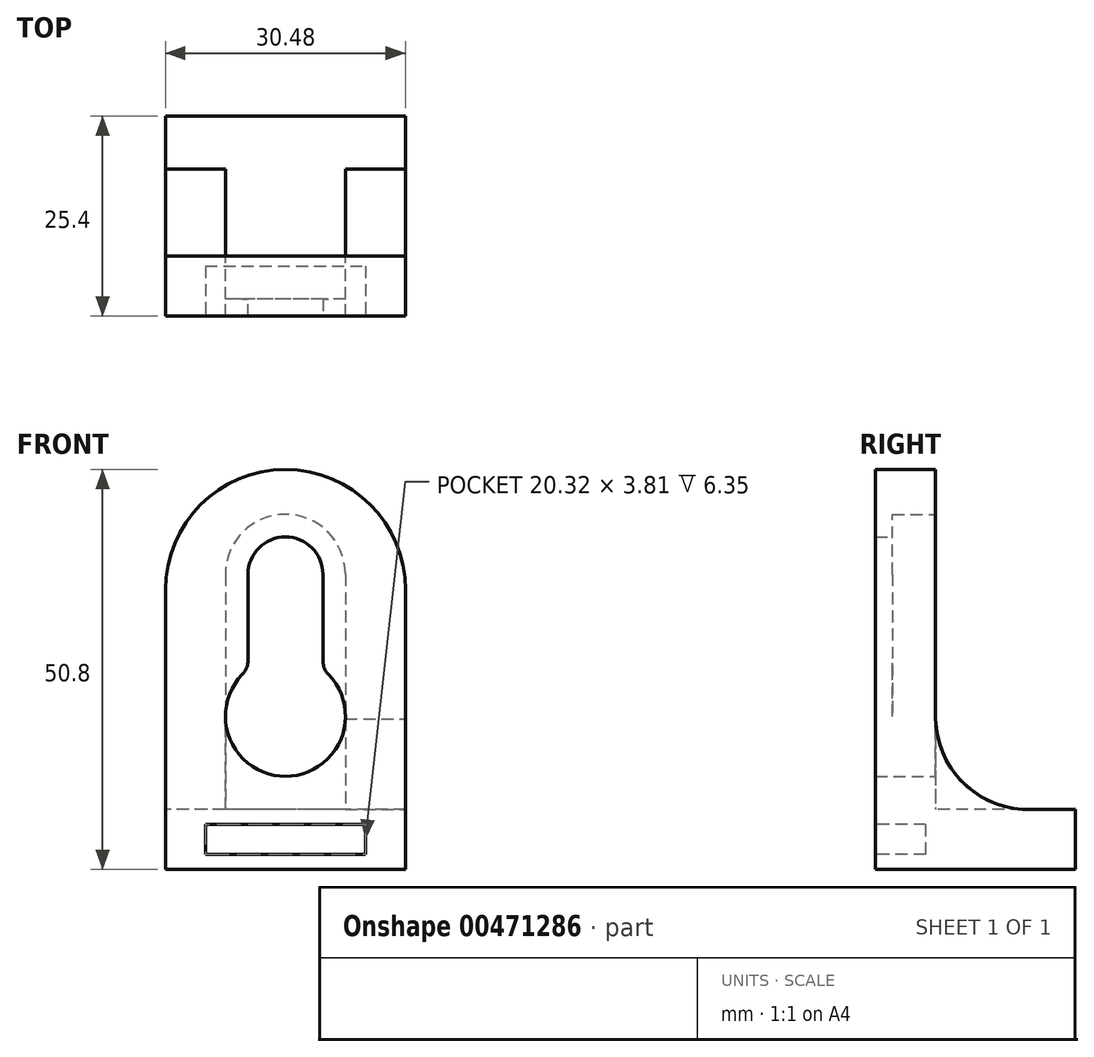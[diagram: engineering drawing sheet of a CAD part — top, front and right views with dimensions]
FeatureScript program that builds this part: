
annotation { "Feature Type Name" : "Feature", "Feature Type Description" : "" }
export const myFeature = defineFeature(function(context is Context, id is Id, definition is map)
    precondition{}
    {
        {
            var Q0;
            Q0=qCreatedBy(makeId("Front.planeOp"),FACE);
            var sketch = newSketch(context, id + "F0", { "sketchPlane" : qUnion([Q0])});
            skLineSegment(sketch, "E0.bottom", {"start": v(-15.24, 25.4) * mm, "end": v(15.24, 25.4) * mm});
            skLineSegment(sketch, "E0.top", {"start": v(-15.24, -25.4) * mm, "end": v(15.24, -25.4) * mm});
            skLineSegment(sketch, "E0.left", {"start": v(-15.24, 25.4) * mm, "end": v(-15.24, -25.4) * mm});
            skLineSegment(sketch, "E0.right", {"start": v(15.24, 25.4) * mm, "end": v(15.24, -25.4) * mm});
            skSolve(sketch);
        }
        {
            var Q0;
            Q0=makeQuery(id+"F0.imprint","IMPRINT",FACE,{"disambiguationData":[TD([[makeQuery(id+"F0.imprint","IMPRINT",EDGE,{"derivedFrom":sQuery(id+"F0.wireOp",EDGE,"E0.bottom")}),-1.0]])]});
            var sketch = newSketch(context, id + "F1", { "sketchPlane" : qUnion([Q0])});
            skArc(sketch, "E1", {"start": v(4.76, 12.09) * mm, "mid": v(0, 16.85) * mm, "end": v(-4.76, 12.09) * mm});
            skArc(sketch, "E2", {"start": v(-4.76, 0) * mm, "mid": v(0, -13.57) * mm, "end": v(4.76, 0) * mm});
            skLineSegment(sketch, "E3", {"start": v(-4.76, 12.09) * mm, "end": v(-4.76, 0) * mm});
            skLineSegment(sketch, "E4", {"start": v(4.76, 12.09) * mm, "end": v(4.76, 0) * mm});
            skArc(sketch, "E5", {"start": v(7.62, 12.09) * mm, "mid": v(0, 19.7) * mm, "end": v(-7.62, 12.09) * mm});
            skLineSegment(sketch, "E6", {"start": v(-7.62, 12.09) * mm, "end": v(-7.62, -5.95) * mm});
            skLineSegment(sketch, "E7", {"start": v(7.62, 12.09) * mm, "end": v(7.62, -5.95) * mm});
            skSolve(sketch);
        }
        {
            var Q0;
            Q0 = qSketchRegion(id + "F0", true);
            extrude(context, id + "F2", {"entities" : qUnion([Q0]), "depth" : 7.62 * mm, "offsetDistance" : 25.4 * mm});
        }
        {
            var Q0;
            Q0=makeQuery(id+"F1.imprint","IMPRINT",FACE,{"disambiguationData":[TD([[makeQuery(id+"F1.imprint","IMPRINT",EDGE,{"derivedFrom":sQuery(id+"F1.wireOp",EDGE,"E1")}),1.0]])]});
            extrude(context, id + "F3", {"entities" : qUnion([Q0]), "operationType" : NewBodyOperationType.REMOVE, "depth" : 7.62 * mm, "offsetDistance" : 25.4 * mm});
        }
        {
            var Q0;
            Q0 = qSketchRegion(id + "F1", true);
            extrude(context, id + "F4", {"entities" : qUnion([Q0]), "operationType" : NewBodyOperationType.REMOVE, "depth" : 5.46 * mm, "offsetDistance" : 25.4 * mm});
        }
        {
            var Q0;
            Q0=makeQuery(id+"F2.opExtrude","CAP_FACE",FACE,{"disambiguationData":[OSD([sQuery(id+"F0.wireOp",EDGE,"E0.bottom"),sQuery(id+"F0.wireOp",EDGE,"E0.top"),sQuery(id+"F0.wireOp",EDGE,"E0.left"),sQuery(id+"F0.wireOp",EDGE,"E0.right")])],"isStart":true});
            var sketch = newSketch(context, id + "F5", { "sketchPlane" : qUnion([Q0])});
            skLineSegment(sketch, "E8.bottom", {"start": v(-15.24, -25.4) * mm, "end": v(15.24, -25.4) * mm});
            skLineSegment(sketch, "E8.top", {"start": v(-15.24, -17.78) * mm, "end": v(15.24, -17.78) * mm});
            skLineSegment(sketch, "E8.left", {"start": v(-15.24, -25.4) * mm, "end": v(-15.24, -17.78) * mm});
            skLineSegment(sketch, "E8.right", {"start": v(15.24, -25.4) * mm, "end": v(15.24, -17.78) * mm});
            skSolve(sketch);
        }
        {
            var Q0;
            Q0 = qSketchRegion(id + "F5", true);
            extrude(context, id + "F6", {"entities" : qUnion([Q0]), "operationType" : NewBodyOperationType.ADD, "depth" : 17.78 * mm, "offsetDistance" : 25.4 * mm});
        }
        {
            var Q0;
            Q0=makeQuery(id+"F6.boolean.opBoolean","MERGE",FACE,{"derivedFrom":[makeQuery(id+"F2.opExtrude","SWEPT_FACE",FACE,{"disambiguationData":[OSD([sQuery(id+"F0.wireOp",EDGE,"E0.right")])]}),makeQuery(id+"F6.opExtrude","SWEPT_FACE",FACE,{"disambiguationData":[OSD([sQuery(id+"F5.wireOp",EDGE,"E8.left")])]})]});
            var sketch = newSketch(context, id + "F7", { "sketchPlane" : qUnion([Q0])});
            skArc(sketch, "E9", {"start": v(0, -6.31) * mm, "mid": v(3.3, -14.18) * mm, "end": v(11.02, -17.78) * mm});
            skLineSegment(sketch, "E10", {"start": v(0, -6.31) * mm, "end": v(0, -17.78) * mm});
            skLineSegment(sketch, "E11", {"start": v(0, -17.78) * mm, "end": v(11.02, -17.78) * mm});
            skSolve(sketch);
        }
        {
            var Q0;
            Q0=makeQuery(id+"F7.imprint","IMPRINT",FACE,{"disambiguationData":[TD([[makeQuery(id+"F7.imprint","IMPRINT",EDGE,{"derivedFrom":sQuery(id+"F7.wireOp",EDGE,"E9")}),-1.0]])]});
            extrude(context, id + "F8", {"entities" : qUnion([Q0]), "operationType" : NewBodyOperationType.ADD, "oppositeDirection" : true, "depth" : 7.62 * mm, "offsetDistance" : 25.4 * mm});
        }
        {
            var Q0;
            Q0=makeQuery(id+"F6.boolean.opBoolean","MERGE",FACE,{"derivedFrom":[makeQuery(id+"F2.opExtrude","SWEPT_FACE",FACE,{"disambiguationData":[OSD([sQuery(id+"F0.wireOp",EDGE,"E0.left")])]}),makeQuery(id+"F6.opExtrude","SWEPT_FACE",FACE,{"disambiguationData":[OSD([sQuery(id+"F5.wireOp",EDGE,"E8.right")])]})]});
            var sketch = newSketch(context, id + "F9", { "sketchPlane" : qUnion([Q0])});
            skLineSegment(sketch, "E12", {"start": v(0, -17.78) * mm, "end": v(-11.02, -17.78) * mm});
            skLineSegment(sketch, "E13", {"start": v(0, -17.78) * mm, "end": v(0, -6) * mm});
            skArc(sketch, "E14", {"start": v(-11.02, -17.78) * mm, "mid": v(-3.19, -14.06) * mm, "end": v(0, -6) * mm});
            skSolve(sketch);
        }
        {
            var Q0;
            Q0=makeQuery(id+"F9.imprint","IMPRINT",FACE,{"disambiguationData":[TD([[makeQuery(id+"F9.imprint","IMPRINT",EDGE,{"derivedFrom":sQuery(id+"F9.wireOp",EDGE,"E12")}),1.0]])]});
            extrude(context, id + "F10", {"entities" : qUnion([Q0]), "operationType" : NewBodyOperationType.ADD, "oppositeDirection" : true, "depth" : 7.62 * mm, "offsetDistance" : 25.4 * mm});
        }
        {
            var Q0;
            Q0=makeQuery(id+"F2.opExtrude","CAP_FACE",FACE,{"disambiguationData":[OSD([sQuery(id+"F0.wireOp",EDGE,"E0.bottom"),sQuery(id+"F0.wireOp",EDGE,"E0.top"),sQuery(id+"F0.wireOp",EDGE,"E0.left"),sQuery(id+"F0.wireOp",EDGE,"E0.right")])],"isStart":false});
            var sketch = newSketch(context, id + "F11", { "sketchPlane" : qUnion([Q0])});
            skLineSegment(sketch, "E15.bottom", {"start": v(-10.16, -19.68) * mm, "end": v(10.16, -19.68) * mm});
            skLineSegment(sketch, "E15.top", {"start": v(-10.16, -23.5) * mm, "end": v(10.16, -23.5) * mm});
            skLineSegment(sketch, "E15.left", {"start": v(-10.16, -19.68) * mm, "end": v(-10.16, -23.5) * mm});
            skLineSegment(sketch, "E15.right", {"start": v(10.16, -19.68) * mm, "end": v(10.16, -23.5) * mm});
            skSolve(sketch);
        }
        {
            var Q0;
            Q0=makeQuery(id+"F11.imprint","IMPRINT",FACE,{"disambiguationData":[TD([[makeQuery(id+"F11.imprint","IMPRINT",EDGE,{"derivedFrom":sQuery(id+"F11.wireOp",EDGE,"E15.bottom")}),-1.0]])]});
            extrude(context, id + "F12", {"entities" : qUnion([Q0]), "operationType" : NewBodyOperationType.REMOVE, "oppositeDirection" : true, "depth" : 6.35 * mm, "offsetDistance" : 25.4 * mm});
        }
        {
            var Q0;
            Q0=makeQuery(id+"F2.opExtrude","SWEPT_EDGE",EDGE,{"disambiguationData":[OSD([sQuery(id+"F0.wireOp",EDGE,"E0.bottom"),sQuery(id+"F0.wireOp",EDGE,"E0.right")])]});
            var Q1;
            Q1=makeQuery(id+"F2.opExtrude","SWEPT_EDGE",EDGE,{"disambiguationData":[OSD([sQuery(id+"F0.wireOp",EDGE,"E0.bottom"),sQuery(id+"F0.wireOp",EDGE,"E0.left")])]});
            fillet(context, id + "F13", {"entities" : qUnion([Q0, Q1]), "radius" : 15.24 * mm, "tangentPropagation" : true, "allowEdgeOverflow" : false});
        }
        {
            var Q0;
            Q0=makeQuery(id+"F3.boolean.opBoolean","COPY",EDGE,{"derivedFrom":makeQuery(id+"F3.opExtrude","SWEPT_EDGE",EDGE,{"disambiguationData":[OSD([sQuery(id+"F1.wireOp",EDGE,"E2"),sQuery(id+"F1.wireOp",EDGE,"E4")])]})});
            var Q1;
            Q1=makeQuery(id+"F3.boolean.opBoolean","COPY",EDGE,{"derivedFrom":makeQuery(id+"F3.opExtrude","SWEPT_EDGE",EDGE,{"disambiguationData":[OSD([sQuery(id+"F1.wireOp",EDGE,"E2"),sQuery(id+"F1.wireOp",EDGE,"E3")])]})});
            fillet(context, id + "F14", {"entities" : qUnion([Q0, Q1]), "radius" : 2.54 * mm, "tangentPropagation" : true, "allowEdgeOverflow" : false});
        }
    });
